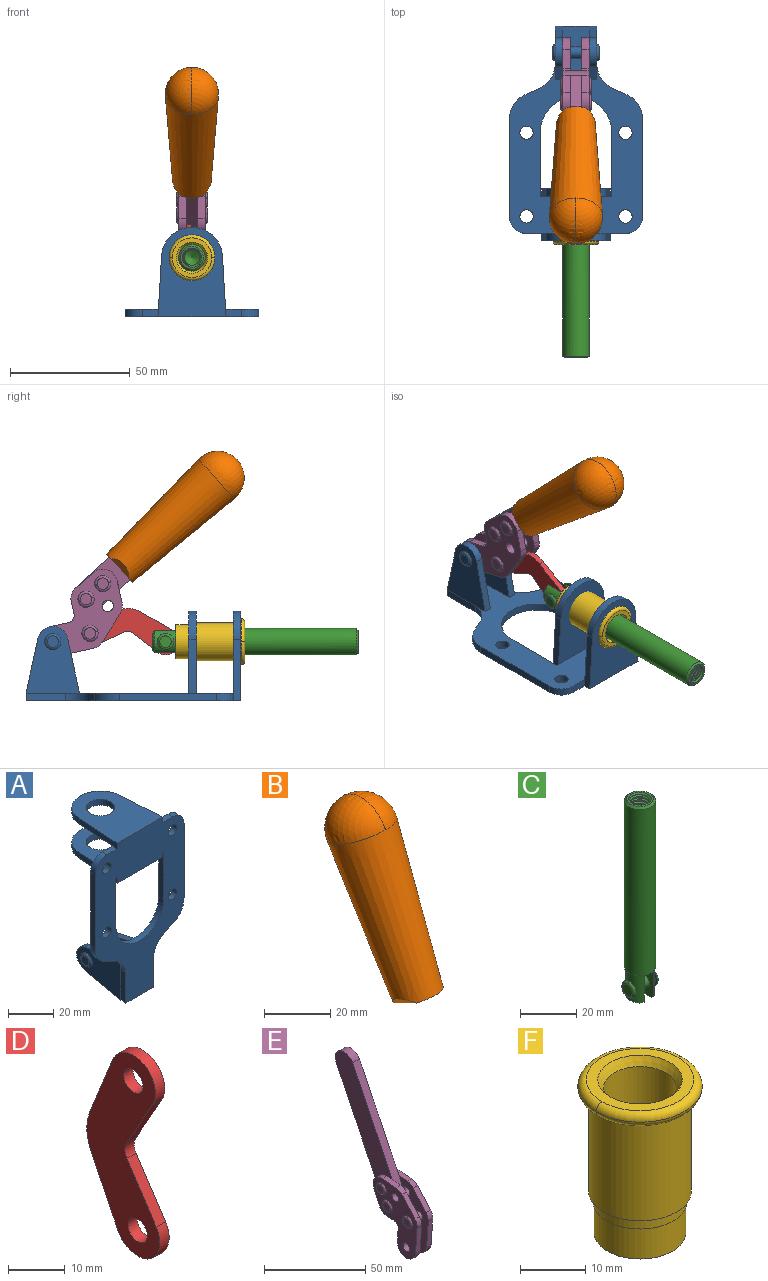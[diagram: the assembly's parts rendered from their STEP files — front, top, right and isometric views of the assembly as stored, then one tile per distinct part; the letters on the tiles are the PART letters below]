
ASSEMBLY  parts=6 mates=6
PART A: 55 faces, bbox 55.7x37.4x89.8 mm
  f0: torus R=2.41mm, axis (-1,0,0), area 15mm2, adj f11,f15,f25
  f1: torus R=2.41mm, axis (-1,0,0), area 15mm2, adj f10,f12,f22
  f2: cylinder r=2.78mm len=5.56mm, axis (0,-1,0), area 54.2mm2, adj f30,f54
  f3: cylinder r=14.99mm len=29.97mm, axis (0,-1,0), area 145.9mm2, adj f30,f49,f53,f54
  f4: cylinder r=2.78mm len=5.56mm, axis (0,-1,0), area 54.2mm2, adj f30,f54
  f5: cylinder r=2.78mm len=5.56mm, axis (0,-1,0), area 54.2mm2, adj f30,f54
  f6: cylinder r=2.78mm len=5.56mm, axis (0,-1,0), area 54.2mm2, adj f30,f54
  f7: cylinder r=6.35mm len=12.7mm, axis (0,0,1), area 123.6mm2, adj f27,f51
  f8: cylinder r=6.35mm len=12.7mm, axis (0,0,-1), area 124.7mm2, adj f21,f35
  f9: cylinder r=2.41mm len=11.18mm, axis (-1,0,0), area 169.4mm2, adj f16,f19
  f10: plane 4.83x4.83mm, normal (1,0,0), area 18.3mm2, adj f1,f12
  f11: plane 4.83x4.83mm, normal (-1,0,0), area 18.3mm2, adj f0,f15
  f12: torus R=2.41mm, axis (-1,0,0), area 15mm2, adj f1,f10,f22
  f13: cylinder r=6.35mm len=12.41mm, axis (1,0,0), area 53.4mm2, adj f18,f19,f22,f23
  f14: cylinder r=6.35mm len=12.41mm, axis (-1,0,0), area 53.4mm2, adj f16,f17,f24,f25
  f15: torus R=2.41mm, axis (-1,0,0), area 15mm2, adj f0,f11,f25
  f16: plane 27.86x22.35mm, normal (1,0,0), area 425.4mm2, adj f9,f14,f17,f24,f30
  f17: plane 22.86x4.97mm, normal (0,0.21,0.98), area 72.5mm2, adj f14,f16,f25,f30
  f18: plane 22.86x4.97mm, normal (0,0.21,0.98), area 72.5mm2, adj f13,f19,f22,f30
  f19: plane 27.86x22.35mm, normal (-1,0,0), area 425.4mm2, adj f9,f13,f18,f23,f30
  f20: cylinder r=12.7mm len=25.35mm, axis (0,0,-1), area 119.8mm2, adj f21,f34,f35,f36
  f21: plane 34.21x28.07mm, normal (0,0,-1), area 702.4mm2, adj f8,f20,f30,f34,f36
  f22: plane 27.96x22.45mm, normal (1,0,0), area 407.2mm2, adj f1,f12,f13,f18,f23,f30,f42,f43
  f23: plane 22.86x4.97mm, normal (0,0.21,-0.98), area 72.5mm2, adj f13,f19,f22,f44
  f24: plane 22.86x4.97mm, normal (0,0.21,-0.98), area 72.5mm2, adj f14,f16,f25,f44
  f25: plane 27.86x22.35mm, normal (-1,0,0), area 407.1mm2, adj f0,f14,f15,f17,f24,f30,f45,f46
  f26: plane 3.1x0.95mm, normal (0,0,-1), area 2.7mm2, adj f30,f49,f50,f54
  f27: plane 34.21x28.07mm, normal (0,0,1), area 702.4mm2, adj f7,f28,f30,f50,f52
  f28: cylinder r=12.7mm len=25.35mm, axis (0,0,1), area 118.8mm2, adj f27,f50,f51,f52
  f29: plane 3.1x0.95mm, normal (0,0,-1), area 2.7mm2, adj f30,f52,f53,f54
  f30: plane 86.54x55.63mm, normal (0,1,0), area 2362.9mm2, adj f2,f3,f4,f5,f6,f16,f17,f18
  f31: plane 40.56x3.1mm, normal (-1,0,0), area 125.7mm2, adj f30,f32,f48,f54
  f32: cylinder r=7.11mm len=7.11mm, axis (0,-1,0), area 34.6mm2, adj f30,f31,f33,f54
  f33: plane 6.67x3.1mm, normal (0,0,1), area 20.4mm2, adj f30,f32,f34,f54
  f34: plane 25.39x3.13mm, normal (-1,0.06,0), area 79.5mm2, adj f20,f21,f33,f35,f54
  f35: plane 37.31x28.45mm, normal (0,0,1), area 789.9mm2, adj f8,f20,f34,f36,f54
  f36: plane 25.39x3.13mm, normal (1,0.06,0), area 79.5mm2, adj f20,f21,f35,f37,f54
  f37: plane 6.67x3.1mm, normal (0,0,1), area 20.4mm2, adj f30,f36,f38,f54
  f38: cylinder r=7.11mm len=7.11mm, axis (0,-1,0), area 34.6mm2, adj f30,f37,f39,f54
  f39: plane 40.56x3.1mm, normal (1,0,0), area 125.7mm2, adj f30,f38,f40,f54
  f40: cylinder r=11.18mm len=10.16mm, axis (0,-1,0), area 39.5mm2, adj f30,f39,f41,f54
  f41: plane 6.09x3.1mm, normal (0.42,0,-0.91), area 20.8mm2, adj f30,f40,f42,f54
  f42: cylinder r=11.18mm len=9.41mm, axis (0,-1,0), area 37.2mm2, adj f22,f30,f41,f43,f54
  f43: plane 16.5x3.1mm, normal (1,0,0), area 51.1mm2, adj f22,f42,f44,f54
  f44: plane 17.37x3.1mm, normal (0,0,-1), area 53.8mm2, adj f23,f24,f30,f43,f45,f54
  f45: plane 16.5x3.1mm, normal (-1,0,0), area 51.1mm2, adj f25,f44,f46,f54
  f46: cylinder r=11.18mm len=9.41mm, axis (0,-1,0), area 37.2mm2, adj f25,f30,f45,f47,f54
  f47: plane 6.09x3.1mm, normal (-0.42,0,-0.91), area 20.8mm2, adj f30,f46,f48,f54
  f48: cylinder r=11.18mm len=10.16mm, axis (0,-1,0), area 39.5mm2, adj f30,f31,f47,f54
  f49: plane 26.54x3.1mm, normal (-1,0,0), area 82.3mm2, adj f3,f26,f30,f54
  f50: plane 25.39x3.1mm, normal (1,0.06,0), area 78.8mm2, adj f26,f27,f28,f51,f54
  f51: plane 37.31x28.45mm, normal (0,0,-1), area 789.9mm2, adj f7,f28,f50,f52,f54
  f52: plane 25.39x3.1mm, normal (-1,0.06,0), area 78.8mm2, adj f27,f28,f29,f51,f54
  f53: plane 26.54x3.1mm, normal (1,0,0), area 82.3mm2, adj f3,f29,f30,f54
  f54: plane 89.66x55.63mm, normal (0,-1,0), area 2678.5mm2, adj f2,f3,f4,f5,f6,f26,f29,f31
PART B: 11 faces, bbox 22.3x42.6x64.5 mm
  f0: sphere r=11.13mm, area 411.4mm2, adj f1,f8
  f1: cone r=11.11mm half-angle=3.3deg, axis (0,0.44,0.9), area 3251.8mm2, adj f0,f7,f8,f9,f10
  f2: cylinder r=6.16mm len=11.7mm, axis (1,0,0), area 89.5mm2, adj f3,f4,f5,f6
  f3: plane 60.23x36.75mm, normal (-1,0,0), area 763.6mm2, adj f2,f4,f6,f10
  f4: plane 51.37x25.05mm, normal (0,0.9,-0.44), area 264.2mm2, adj f2,f3,f5,f10
  f5: plane 60.23x36.75mm, normal (1,0,0), area 763.6mm2, adj f2,f4,f6,f10
  f6: plane 51.37x25.05mm, normal (0,-0.9,0.44), area 264.2mm2, adj f2,f3,f5,f10
  f7: plane 9.95x5.95mm, normal (0.71,-0.31,-0.64), area 25.8mm2, adj f1,f10
  f8: sphere r=11.13mm, area 411.4mm2, adj f0,f1
  f9: plane 9.95x5.95mm, normal (-0.71,-0.31,-0.64), area 25.8mm2, adj f1,f10
  f10: plane 14.27x11.38mm, normal (0,-0.44,-0.9), area 106.7mm2, adj f1,f3,f4,f5,f6,f7,f9
PART C: 48 faces, bbox 12.6x11.1x86.1 mm
  f0: torus R=2.41mm, axis (-1,0,0), area 15mm2, adj f30,f32,f34
  f1: torus R=2.41mm, axis (-1,0,0), area 15mm2, adj f29,f31,f33
  f2: cylinder r=5.54mm len=72.39mm, axis (0,0,1), area 2518.5mm2, adj f3,f4,f42,f43
  f3: cone r=5.54mm half-angle=45deg, axis (0,0,1), area 7.6mm2, adj f2,f5,f41
  f4: cone r=5.54mm half-angle=45deg, axis (0,0,-1), area 34.9mm2, adj f2,f39
  f5: cylinder r=5.08mm len=11.48mm, axis (0,0,1), area 108.3mm2, adj f3,f7,f8,f41
  f6: cylinder r=2.41mm len=4.83mm, axis (-1,0,0), area 71.2mm2, adj f40,f41
  f7: cylinder r=2.41mm len=4.83mm, axis (-1,0,0), area 7.6mm2, adj f5,f34
  f8: cone r=5.08mm half-angle=45deg, axis (0,0,1), area 10.6mm2, adj f5,f37,f41
  f9: cone r=3.98mm half-angle=45deg, axis (0,0,1), area 17.6mm2, adj f27,f39,f45,f46,f47
  f10: cylinder r=2.41mm len=4.83mm, axis (-1,0,0), area 7.6mm2, adj f33,f38
  f11: cylinder r=3.2mm len=6.4mm, axis (0,0,1), area 78.4mm2, adj f12,f28,f44,f45,f47
  f12: cylinder r=3.2mm len=6.4mm, axis (0,0,1), area 10.5mm2, adj f11,f13,f45,f47
  f13: cylinder r=3.2mm len=6.4mm, axis (0,0,1), area 10.5mm2, adj f12,f14,f45,f47
  f14: cylinder r=3.2mm len=6.4mm, axis (0,0,1), area 10.5mm2, adj f13,f15,f45,f47
  f15: cylinder r=3.2mm len=6.4mm, axis (0,0,1), area 10.5mm2, adj f14,f16,f45,f47
  f16: cylinder r=3.2mm len=6.4mm, axis (0,0,1), area 10.5mm2, adj f15,f17,f45,f47
  f17: cylinder r=3.2mm len=6.4mm, axis (0,0,1), area 10.5mm2, adj f16,f18,f45,f47
  f18: cylinder r=3.2mm len=6.4mm, axis (0,0,1), area 10.5mm2, adj f17,f19,f45,f47
  f19: cylinder r=3.2mm len=6.4mm, axis (0,0,1), area 10.5mm2, adj f18,f20,f45,f47
  f20: cylinder r=3.2mm len=6.4mm, axis (0,0,1), area 10.5mm2, adj f19,f21,f45,f47
  f21: cylinder r=3.2mm len=6.4mm, axis (0,0,1), area 10.5mm2, adj f20,f22,f45,f47
  f22: cylinder r=3.2mm len=6.4mm, axis (0,0,1), area 10.5mm2, adj f21,f23,f45,f47
  f23: cylinder r=3.2mm len=6.4mm, axis (0,0,1), area 10.5mm2, adj f22,f24,f45,f47
  f24: cylinder r=3.2mm len=6.4mm, axis (0,0,1), area 10.5mm2, adj f23,f25,f45,f47
  f25: cylinder r=3.2mm len=6.4mm, axis (0,0,1), area 10.5mm2, adj f24,f26,f45,f47
  f26: cylinder r=3.2mm len=6.4mm, axis (0,0,1), area 10.5mm2, adj f25,f27,f45,f47
  f27: cylinder r=3.2mm len=6.4mm, axis (0,0,1), area 7.4mm2, adj f9,f26,f45,f47
  f28: cone r=3.2mm half-angle=60deg, axis (0,0,1), area 37.2mm2, adj f11
  f29: plane 4.83x4.83mm, normal (-1,0,0), area 18.3mm2, adj f1,f31
  f30: plane 4.83x4.83mm, normal (1,0,0), area 18.3mm2, adj f0,f32
  f31: torus R=2.41mm, axis (-1,0,0), area 15mm2, adj f1,f29,f33
  f32: torus R=2.41mm, axis (-1,0,0), area 15mm2, adj f0,f30,f34
  f33: plane 6.83x6.83mm, normal (1,0,0), area 18.3mm2, adj f1,f10,f31
  f34: plane 6.83x6.83mm, normal (-1,0,0), area 18.3mm2, adj f0,f7,f32
  f35: cone r=5.08mm half-angle=45deg, axis (0,0,1), area 10.6mm2, adj f36,f38,f40
  f36: plane 7.25x1.97mm, normal (0,0,-1), area 10mm2, adj f35,f40
  f37: plane 7.25x1.97mm, normal (0,0,-1), area 10mm2, adj f8,f41
  f38: cylinder r=5.08mm len=11.48mm, axis (0,0,1), area 108.3mm2, adj f10,f35,f40,f42
  f39: plane 9.55x9.55mm, normal (0,0,1), area 22mm2, adj f4,f9
  f40: plane 12.76x10.09mm, normal (1,0,0), area 95.7mm2, adj f6,f35,f36,f38,f42,f43
  f41: plane 12.76x10.09mm, normal (-1,0,0), area 95.7mm2, adj f3,f5,f6,f8,f37,f43
  f42: cone r=5.54mm half-angle=45deg, axis (0,0,1), area 7.6mm2, adj f2,f38,f40
  f43: plane 11.07x4.7mm, normal (0,0,-1), area 50.4mm2, adj f2,f40,f41
  f44: plane 0.89x0.62mm, normal (-1,0,0), area 0.3mm2, adj f11,f45,f46,f47
  f45: bspline ~24.8x7.63mm, area 266.6mm2, adj f9,f11,f12,f13,f14,f15,f16,f17
  f46: bspline ~24.87x7.63mm, area 73.6mm2, adj f9,f44,f45,f47
  f47: bspline ~24.98x7.63mm, area 272.5mm2, adj f9,f11,f12,f13,f14,f15,f16,f17
PART D: 12 faces, bbox 2.3x18.2x42.8 mm
  f0: cylinder r=2.4mm len=4.8mm, axis (1,0,0), area 34.9mm2, adj f4,f11
  f1: cylinder r=10.41mm len=8.47mm, axis (1,0,0), area 20.2mm2, adj f4,f9,f10,f11
  f2: cylinder r=3.05mm len=3.16mm, axis (1,0,0), area 7.7mm2, adj f4,f6,f7,f11
  f3: cylinder r=2.4mm len=4.8mm, axis (1,0,0), area 34.9mm2, adj f4,f11
  f4: plane 42.81x18.23mm, normal (-1,0,0), area 414.1mm2, adj f0,f1,f2,f3,f5,f6,f7,f8
  f5: cylinder r=5.54mm len=10.67mm, axis (1,0,0), area 41.8mm2, adj f4,f6,f10,f11
  f6: plane 11.66x6.53mm, normal (0,-0.87,-0.49), area 30.9mm2, adj f2,f4,f5,f11
  f7: plane 11.17x7.33mm, normal (0,-0.84,0.55), area 30.9mm2, adj f2,f4,f8,f11
  f8: cylinder r=5.54mm len=10.51mm, axis (1,0,0), area 41.8mm2, adj f4,f7,f9,f11
  f9: plane 13.67x6.67mm, normal (0,0.9,-0.44), area 35.1mm2, adj f1,f4,f8,f11
  f10: plane 14.1x5.7mm, normal (0,0.93,0.37), area 35.1mm2, adj f1,f4,f5,f11
  f11: plane 42.81x18.23mm, normal (1,0,0), area 414.1mm2, adj f0,f1,f2,f3,f5,f6,f7,f8
PART E: 59 faces, bbox 12.9x60.2x99.6 mm
  f0: torus R=2.39mm, axis (-1,0,0), area 14.9mm2, adj f20,f43,f51
  f1: torus R=2.39mm, axis (-1,0,0), area 14.9mm2, adj f19,f42,f51
  f2: torus R=2.39mm, axis (-1,0,0), area 14.9mm2, adj f18,f35,f51
  f3: torus R=2.39mm, axis (-1,0,0), area 14.9mm2, adj f14,f17,f23
  f4: torus R=2.39mm, axis (-1,0,0), area 14.9mm2, adj f13,f16,f23
  f5: torus R=2.39mm, axis (-1,0,0), area 14.9mm2, adj f12,f15,f23
  f6: cylinder r=2.39mm len=4.78mm, axis (1,0,0), area 46.5mm2, adj f48,f50,f51
  f7: cylinder r=2.39mm len=4.78mm, axis (1,0,0), area 46.5mm2, adj f50,f51
  f8: cylinder r=6.35mm len=12.68mm, axis (1,0,0), area 61.8mm2, adj f38,f39,f50,f51
  f9: cylinder r=2.39mm len=4.78mm, axis (-1,0,0), area 70.5mm2, adj f46,f50
  f10: cylinder r=2.39mm len=4.78mm, axis (-1,0,0), area 46.5mm2, adj f23,f45,f46
  f11: cylinder r=2.39mm len=4.78mm, axis (-1,0,0), area 46.5mm2, adj f23,f46
  f12: plane 4.78x4.78mm, normal (1,0,0), area 17.9mm2, adj f5,f15
  f13: plane 4.78x4.78mm, normal (1,0,0), area 17.9mm2, adj f4,f16
  f14: plane 4.78x4.78mm, normal (1,0,0), area 17.9mm2, adj f3,f17
  f15: torus R=2.39mm, axis (-1,0,0), area 14.9mm2, adj f5,f12,f23
  f16: torus R=2.39mm, axis (-1,0,0), area 14.9mm2, adj f4,f13,f23
  f17: torus R=2.39mm, axis (-1,0,0), area 14.9mm2, adj f3,f14,f23
  f18: plane 4.78x4.78mm, normal (-1,0,0), area 17.9mm2, adj f2,f35
  f19: plane 4.78x4.78mm, normal (-1,0,0), area 17.9mm2, adj f1,f42
  f20: plane 4.78x4.78mm, normal (-1,0,0), area 17.9mm2, adj f0,f43
  f21: plane 2.26x0.2mm, normal (1,0,0), area 0.2mm2, adj f31,f44
  f22: plane 2.26x0.2mm, normal (-1,0,0), area 0.2mm2, adj f41,f44
  f23: plane 39.37x30.77mm, normal (1,0,0), area 565.5mm2, adj f3,f4,f5,f10,f11,f15,f16,f17
  f24: cylinder r=6.1mm len=4.15mm, axis (-1,0,0), area 14.7mm2, adj f23,f25,f32,f46
  f25: plane 10.25x9.01mm, normal (0,-0.75,0.66), area 42.3mm2, adj f23,f24,f26,f46
  f26: cylinder r=6.35mm len=4.64mm, axis (-1,0,0), area 15.6mm2, adj f23,f25,f27,f46
  f27: plane 15.84x3.1mm, normal (0,-1,-0.07), area 49.2mm2, adj f23,f26,f28,f46
  f28: cylinder r=6.35mm len=12.68mm, axis (-1,0,0), area 61.8mm2, adj f23,f27,f29,f46
  f29: plane 8.11x3.1mm, normal (0,1,0.07), area 25.2mm2, adj f23,f28,f30,f46
  f30: cylinder r=3.05mm len=3.25mm, axis (-1,0,0), area 14.8mm2, adj f23,f29,f31,f46
  f31: plane 5.99x3.1mm, normal (0,0.07,-1), area 18.6mm2, adj f21,f23,f30,f44,f46
  f32: plane 9.5x3.1mm, normal (0,-0.07,1), area 29.5mm2, adj f23,f24,f33,f46,f47
  f33: cylinder r=6.1mm len=8.63mm, axis (-1,0,0), area 39.1mm2, adj f23,f32,f34,f47
  f34: plane 8.65x3.96mm, normal (0,0.91,-0.42), area 29.5mm2, adj f23,f33,f44,f47
  f35: torus R=2.39mm, axis (-1,0,0), area 14.9mm2, adj f2,f18,f51
  f36: plane 10.25x9.01mm, normal (0,-0.75,0.66), area 42.3mm2, adj f37,f49,f50,f51
  f37: cylinder r=6.35mm len=4.64mm, axis (1,0,0), area 15.6mm2, adj f36,f38,f50,f51
  f38: plane 15.84x3.1mm, normal (0,-1,-0.07), area 49.2mm2, adj f8,f37,f50,f51
  f39: plane 8.11x3.1mm, normal (0,1,0.07), area 25.2mm2, adj f8,f40,f50,f51
  f40: cylinder r=3.05mm len=3.25mm, axis (1,0,0), area 14.8mm2, adj f39,f41,f50,f51
  f41: plane 5.99x3.1mm, normal (0,0.07,-1), area 18.6mm2, adj f22,f40,f44,f50,f51
  f42: torus R=2.39mm, axis (-1,0,0), area 14.9mm2, adj f1,f19,f51
  f43: torus R=2.39mm, axis (-1,0,0), area 14.9mm2, adj f0,f20,f51
  f44: cylinder r=6.35mm len=12.12mm, axis (-1,0,0), area 128.9mm2, adj f21,f22,f23,f31,f34,f41,f46,f47
  f45: plane 2.65x1.35mm, normal (1,0,0), area 1mm2, adj f10,f55
  f46: plane 39.08x20.42mm, normal (-1,0,0), area 412.5mm2, adj f9,f10,f11,f24,f25,f26,f27,f28
  f47: plane 77.62x39.82mm, normal (1,0,0), area 850mm2, adj f32,f33,f34,f44,f53,f54,f55
  f48: plane 2.65x1.35mm, normal (-1,0,0), area 1mm2, adj f6,f55
  f49: cylinder r=6.1mm len=4.15mm, axis (1,0,0), area 14.7mm2, adj f36,f50,f51,f56
  f50: plane 39.08x20.42mm, normal (1,0,0), area 412.5mm2, adj f6,f7,f8,f9,f36,f37,f38,f39
  f51: plane 39.37x30.77mm, normal (-1,0,0), area 565.5mm2, adj f0,f1,f2,f6,f7,f8,f35,f36
  f52: plane 8.65x3.96mm, normal (0,0.91,-0.42), area 29.5mm2, adj f44,f51,f57,f58
  f53: plane 68.49x33.4mm, normal (0,0.9,-0.44), area 358.1mm2, adj f44,f47,f54,f58
  f54: cylinder r=6.35mm len=12.06mm, axis (1,0,0), area 93.7mm2, adj f47,f53,f55,f58
  f55: plane 68.49x33.4mm, normal (0,-0.9,0.44), area 358.1mm2, adj f44,f45,f46,f47,f48,f50,f54,f58
  f56: plane 9.5x3.1mm, normal (0,-0.07,1), area 29.5mm2, adj f49,f50,f51,f57,f58
  f57: cylinder r=6.1mm len=8.63mm, axis (1,0,0), area 39.1mm2, adj f51,f52,f56,f58
  f58: plane 77.62x39.82mm, normal (-1,0,0), area 850mm2, adj f44,f52,f53,f54,f55,f56,f57
PART F: 15 faces, bbox 20.6x20.6x28.7 mm
  f0: torus R=8.26mm, axis (0,0,1), area 56.8mm2, adj f1,f10,f12
  f1: torus R=8.26mm, axis (0,0,1), area 56.8mm2, adj f0,f6,f13
  f2: cylinder r=5.59mm len=25.91mm, axis (0,0,1), area 909.6mm2, adj f3,f4
  f3: cone r=6.86mm half-angle=45deg, axis (0,0,-1), area 70.2mm2, adj f2,f14
  f4: cone r=6.47mm half-angle=30deg, axis (0,0,1), area 66.7mm2, adj f2,f13
  f5: cylinder r=7.04mm len=14.07mm, axis (0,0,1), area 252.6mm2, adj f11,f14
  f6: torus R=8.26mm, axis (0,0,1), area 56.8mm2, adj f1,f12,f13
  f7: cylinder r=7.16mm len=14.33mm, axis (0,0,1), area 91.5mm2, adj f9,f11
  f8: cylinder r=7.86mm len=18.42mm, axis (0,0,1), area 909.6mm2, adj f9,f10
  f9: plane 15.72x15.72mm, normal (0,0,-1), area 33mm2, adj f7,f8
  f10: plane 16.51x16.51mm, normal (0,0,-1), area 19.9mm2, adj f0,f8,f12
  f11: plane 14.33x14.33mm, normal (0,0,-1), area 5.7mm2, adj f5,f7
  f12: torus R=8.26mm, axis (0,0,1), area 56.8mm2, adj f0,f6,f10
  f13: plane 16.51x16.51mm, normal (0,0,1), area 82.7mm2, adj f1,f4,f6
  f14: plane 14.07x14.07mm, normal (0,0,-1), area 7.8mm2, adj f3,f5
PLACE A rot(axis=(1,0,0),90deg) t=(0,9.14,0)mm fixed
PLACE B rot(axis=(1,0,0),73.3deg) t=(-0.04,3.43,10.24)mm
PLACE C rot(axis=(1,0,0),90deg) t=(0,9.66,0)mm
PLACE D rot(axis=(1,0,0),98.3deg) t=(-1.16,13.05,2.49)mm
PLACE E rot(axis=(1,0,0),73.3deg) t=(0,3.43,10.24)mm
PLACE F rot(axis=(1,0,0),90deg) t=(0,10.16,0)mm
MATE revolute C.f6 <-> D.f5  axis (-1,0,0) through (0,-5.81,24.61)mm
MATE fastened B.f2 <-> E.f54  axis (1,0,0) through (-2.35,-28.66,94.01)mm
MATE revolute D.f3 <-> E.f4  axis (-1,0,0) through (0,25.74,28.09)mm
MATE slider F.f2 <-> C.f2  axis (0,-1,0) through (0,-37.25,24.61)mm
MATE revolute E.f7 <-> A.f0  axis (-1,0,0) through (0,41.23,24.61)mm
MATE fastened F.f2 <-> A.f7  axis (0,-1,0) through (0,-37.25,24.61)mm
